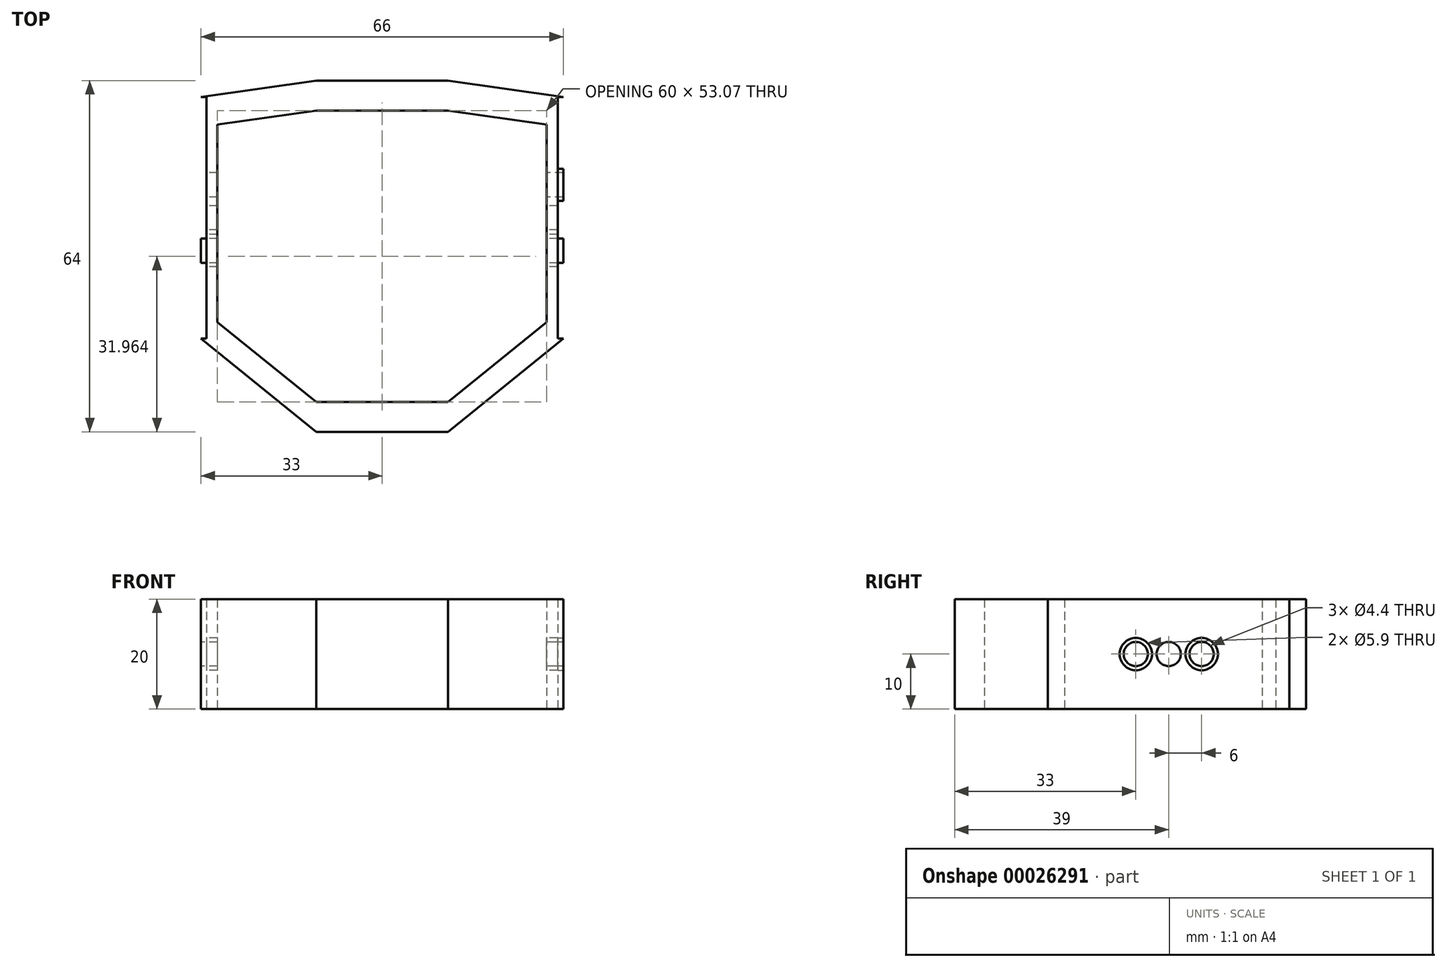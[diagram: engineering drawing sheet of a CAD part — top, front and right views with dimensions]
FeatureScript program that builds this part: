
annotation { "Feature Type Name" : "Feature", "Feature Type Description" : "" }
export const myFeature = defineFeature(function(context is Context, id is Id, definition is map)
    precondition{}
    {
        {
            var Q0;
            Q0=qCreatedBy(makeId("Top.planeOp"),FACE);
            var sketch = newSketch(context, id + "F0", { "sketchPlane" : qUnion([Q0])});
            skPoint(sketch, "E0", {"position": v(-12, 0) * mm});
            skPoint(sketch, "E1", {"position": v(12, 0) * mm});
            skLineSegment(sketch, "E2", {"start": v(-12, 0) * mm, "end": v(12, 0) * mm, "construction": true});
            skLineSegment(sketch, "E3", {"start": v(-12, 0) * mm, "end": v(-12, 36) * mm, "construction": true});
            skLineSegment(sketch, "E4", {"start": v(-12, 36) * mm, "end": v(12, 36) * mm, "construction": true});
            skLineSegment(sketch, "E5", {"start": v(12, 36) * mm, "end": v(12, 0) * mm, "construction": true});
            skLineSegment(sketch, "E6", {"start": v(-12, 36) * mm, "end": v(-30, 36) * mm, "construction": true});
            skLineSegment(sketch, "E7.MirrorCS", {"start": v(12, 36) * mm, "end": v(30, 36) * mm, "construction": true});
            skLineSegment(sketch, "E8", {"start": v(-30, 36) * mm, "end": v(-30, 0) * mm});
            skLineSegment(sketch, "E9", {"start": v(-30, 0) * mm, "end": v(-12, 0) * mm, "construction": true});
            skLineSegment(sketch, "E10", {"start": v(30, 36) * mm, "end": v(30, 0) * mm, "construction": true});
            skLineSegment(sketch, "E11", {"start": v(30, 0) * mm, "end": v(12, 0) * mm, "construction": true});
            skLineSegment(sketch, "E12", {"start": v(-33, 36) * mm, "end": v(-33, -3) * mm});
            skLineSegment(sketch, "E13", {"start": v(-12, 0) * mm, "end": v(-12, -35.4) * mm, "construction": true});
            skPoint(sketch, "E14", {"position": v(-12, -20) * mm});
            skLineSegment(sketch, "E15", {"start": v(-33, -3) * mm, "end": v(-12, -20) * mm});
            skLineSegment(sketch, "E16", {"start": v(-30, 0) * mm, "end": v(-12, -14.57) * mm});
            skLineSegment(sketch, "E17.MirrorCS", {"start": v(30, 36) * mm, "end": v(30, 0) * mm});
            skLineSegment(sketch, "E18.MirrorCS", {"start": v(33, 36) * mm, "end": v(33, -3) * mm});
            skLineSegment(sketch, "E19.MirrorCS", {"start": v(33, -3) * mm, "end": v(12, -20) * mm});
            skLineSegment(sketch, "E20.MirrorCS", {"start": v(30, 0) * mm, "end": v(12, -14.57) * mm});
            skLineSegment(sketch, "E21", {"start": v(-12, -14.57) * mm, "end": v(12, -14.57) * mm});
            skLineSegment(sketch, "E22", {"start": v(-12, -20) * mm, "end": v(12, -20) * mm});
            skLineSegment(sketch, "E23", {"start": v(-12, 36) * mm, "end": v(-12, 38.5) * mm, "construction": true});
            skPoint(sketch, "E24", {"position": v(-12, 44) * mm});
            skLineSegment(sketch, "E25", {"start": v(-30, 36) * mm, "end": v(-12, 36) * mm});
            skLineSegment(sketch, "E26", {"start": v(-33, 36) * mm, "end": v(-33, 41) * mm});
            skLineSegment(sketch, "E27", {"start": v(-33, 41) * mm, "end": v(-12, 44) * mm});
            skLineSegment(sketch, "E28", {"start": v(-30, 36) * mm, "end": v(-12, 38.5) * mm});
            skPoint(sketch, "E28.endSnap0", {"position": v(-33, 38.5) * mm});
            skLineSegment(sketch, "E29.MirrorCS", {"start": v(30, 36) * mm, "end": v(12, 38.5) * mm});
            skLineSegment(sketch, "E30.MirrorCS", {"start": v(33, 41) * mm, "end": v(12, 44) * mm});
            skLineSegment(sketch, "E31.MirrorCS", {"start": v(33, 36) * mm, "end": v(33, 41) * mm});
            skLineSegment(sketch, "E32.trimOffspring", {"start": v(-12, 44) * mm, "end": v(-12, 51.76) * mm, "construction": true});
            skPoint(sketch, "E33.MirrorCS.end.orphan", {"position": v(12, 44) * mm});
            skPoint(sketch, "E33.MirrorCS.start.orphan", {"position": v(12, 38.5) * mm});
            skLineSegment(sketch, "E34", {"start": v(-12, 38.5) * mm, "end": v(12, 38.5) * mm});
            skLineSegment(sketch, "E35", {"start": v(-12, 44) * mm, "end": v(12, 44) * mm});
            skSolve(sketch);
        }
        {
            var Q0;
            Q0=makeQuery(id+"F0.imprint","IMPRINT",FACE,{"disambiguationData":[TD([[makeQuery(id+"F0.imprint","IMPRINT",EDGE,{"derivedFrom":sQuery(id+"F0.wireOp",EDGE,"E8")}),-1.0]])]});
            extrude(context, id + "F1", {"entities" : qUnion([Q0]), "depth" : 20 * mm});
        }
        {
            var Q0;
            Q0=makeQuery(id+"F1.opExtrude","SWEPT_FACE",FACE,{"disambiguationData":[OSD([sQuery(id+"F0.wireOp",EDGE,"E18.MirrorCS"),sQuery(id+"F0.wireOp",EDGE,"E31.MirrorCS")])]});
            var sketch = newSketch(context, id + "F2", { "sketchPlane" : qUnion([Q0])});
            skLineSegment(sketch, "E36", {"start": v(-3, 10) * mm, "end": v(41, 10) * mm, "construction": true});
            skCircle(sketch, "E37", {"center": v(19, 10) * mm, "radius": 2.95 * mm});
            skCircle(sketch, "E38", {"center": v(19, 10) * mm, "radius": 2.2 * mm});
            skCircle(sketch, "E39", {"center": v(13, 10) * mm, "radius": 2.95 * mm});
            skLineSegment(sketch, "E40", {"start": v(19, 10) * mm, "end": v(19, 0) * mm, "construction": true});
            skCircle(sketch, "E41", {"center": v(13, 10) * mm, "radius": 2.2 * mm});
            skCircle(sketch, "E42.MirrorC", {"center": v(25, 10) * mm, "radius": 2.95 * mm});
            skCircle(sketch, "E43.MirrorC", {"center": v(25, 10) * mm, "radius": 2.2 * mm});
            skSolve(sketch);
        }
        {
            var Q0;
            Q0=makeQuery(id+"F1.opExtrude","SWEPT_FACE",FACE,{"disambiguationData":[OSD([sQuery(id+"F0.wireOp",EDGE,"E12"),sQuery(id+"F0.wireOp",EDGE,"E26")])]});
            var sketch = newSketch(context, id + "F3", { "sketchPlane" : qUnion([Q0])});
            skLineSegment(sketch, "E44", {"start": v(-41, 10) * mm, "end": v(3, 10) * mm, "construction": true});
            skCircle(sketch, "E45", {"center": v(-19, 10) * mm, "radius": 2.95 * mm});
            skCircle(sketch, "E46", {"center": v(-19, 10) * mm, "radius": 2.2 * mm});
            skCircle(sketch, "E47", {"center": v(-25, 10) * mm, "radius": 2.95 * mm});
            skLineSegment(sketch, "E48", {"start": v(-19, 10) * mm, "end": v(-19, 0.63) * mm, "construction": true});
            skCircle(sketch, "E49", {"center": v(-25, 10) * mm, "radius": 2.2 * mm});
            skCircle(sketch, "E50.MirrorC", {"center": v(-13, 10) * mm, "radius": 2.95 * mm});
            skCircle(sketch, "E51.MirrorC", {"center": v(-13, 10) * mm, "radius": 2.2 * mm});
            skSolve(sketch);
        }
        {
            var Q0;
            Q0=makeQuery(id+"F3.imprint","IMPRINT",FACE,{"disambiguationData":[TD([[makeQuery(id+"F3.imprint","IMPRINT",EDGE,{"derivedFrom":sQuery(id+"F3.wireOp",EDGE,"E49")}),1.0]])]});
            var Q1;
            Q1=makeQuery(id+"F3.imprint","IMPRINT",FACE,{"disambiguationData":[TD([[makeQuery(id+"F3.imprint","IMPRINT",EDGE,{"derivedFrom":sQuery(id+"F3.wireOp",EDGE,"E46")}),1.0]])]});
            var Q2;
            Q2=makeQuery(id+"F3.imprint","IMPRINT",FACE,{"disambiguationData":[TD([[makeQuery(id+"F3.imprint","IMPRINT",EDGE,{"derivedFrom":sQuery(id+"F3.wireOp",EDGE,"E51.MirrorC")}),-1.0]])]});
            extrude(context, id + "F4", {"entities" : qUnion([Q0, Q1, Q2]), "operationType" : NewBodyOperationType.REMOVE, "endBound" : BoundingType.THROUGH_ALL, "oppositeDirection" : true, "depth" : 25 * mm});
        }
        {
            var Q0;
            Q0=makeQuery(id+"F3.imprint","IMPRINT",FACE,{"disambiguationData":[TD([[makeQuery(id+"F3.imprint","IMPRINT",EDGE,{"derivedFrom":sQuery(id+"F3.wireOp",EDGE,"E50.MirrorC")}),-1.0]])]});
            var Q1;
            Q1=makeQuery(id+"F3.imprint","IMPRINT",FACE,{"disambiguationData":[TD([[makeQuery(id+"F3.imprint","IMPRINT",EDGE,{"derivedFrom":sQuery(id+"F3.wireOp",EDGE,"E45")}),1.0]])]});
            var Q2;
            Q2=makeQuery(id+"F3.imprint","IMPRINT",FACE,{"disambiguationData":[TD([[makeQuery(id+"F3.imprint","IMPRINT",EDGE,{"derivedFrom":sQuery(id+"F3.wireOp",EDGE,"E47")}),1.0]])]});
            extrude(context, id + "F5", {"entities" : qUnion([Q0, Q1, Q2]), "operationType" : NewBodyOperationType.REMOVE, "oppositeDirection" : true, "depth" : 1 * mm});
        }
        {
            var Q0;
            Q0=makeQuery(id+"F2.imprint","IMPRINT",FACE,{"disambiguationData":[TD([[makeQuery(id+"F2.imprint","IMPRINT",EDGE,{"derivedFrom":sQuery(id+"F2.wireOp",EDGE,"E39")}),1.0]])]});
            var Q1;
            Q1=makeQuery(id+"F2.imprint","IMPRINT",FACE,{"disambiguationData":[TD([[makeQuery(id+"F2.imprint","IMPRINT",EDGE,{"derivedFrom":sQuery(id+"F2.wireOp",EDGE,"E37")}),1.0]])]});
            var Q2;
            Q2=makeQuery(id+"F2.imprint","IMPRINT",FACE,{"disambiguationData":[TD([[makeQuery(id+"F2.imprint","IMPRINT",EDGE,{"derivedFrom":sQuery(id+"F2.wireOp",EDGE,"E42.MirrorC")}),-1.0]])]});
            extrude(context, id + "F6", {"entities" : qUnion([Q0, Q1, Q2]), "operationType" : NewBodyOperationType.REMOVE, "oppositeDirection" : true, "depth" : 1 * mm});
        }
    });
